# Revit family: TR2163
name_source: partatom
category: Verbindungsmittel
units: mm (PartAtom-declared; Revit-internal decimal feet)

## family parameters
Arbeitsebenenbasiert = Nein
Beim Laden mit Abzugskörper schneiden = Nein
Gemeinsam genutzt = Nein
Immer vertikal = Nein
OmniClass-Nummer = 23.25.10.27.11.21
OmniClass-Titel = Reinforcement Couplers

## types (10) — shared parameters
Endenbearbeitung 1 = Mit Gewinde
Endenbearbeitung 2 = Mit Gewinde
Hersteller = Stahlwerk Annahütte Max Aicher GmbH Co.KG
Modell = TR 2163
Stabgröße 2 = Keine
TR2163-G_Vis = Ja
TR2163-L_Vis = Ja
TR2163-SW_Vis = Ja
Typenbild = TR2163.png
Typenkommentare = TR 2163 - Ankermutter mit Bund
URL = http//:www.annahuette.com
zero-valued in all types: Einfassung Stab 2

## per-type parameters (varying)
| type | Außendurchmesser | Beschreibung | Einfassung Stab 1 | Gesamtlänge | Körper | Stabgröße 1 | TR2163-G | TR2163-L | TR2163-L1 | TR2163-Ld | TR2163-Lsw | TR2163-SW | TR2163-ø | TR2163-ød |
| TR 2163-ø18 | 36 mm  [stored 0.11811 ft] | TR2163-ø18 | 34 mm | 45 mm  [stored 0.147638 ft] | 0,31 kg | SAS 670 - ø18 | 0,31 kg | 45 mm  [stored 0.147638 ft] | 34 mm | 11 mm  [stored 0.0360892 ft] | 34 mm | 36 mm  [stored 0.11811 ft] | 42 mm  [stored 0.137795 ft] | 18 mm  [stored 0.0590551 ft] |
| TR 2163-ø22 | 41 mm  [stored 0.134514 ft] | TR2163-ø22 | 38 mm  [stored 0.124672 ft] | 50 mm  [stored 0.164042 ft] | 0,43 kg | SAS 670 - ø22 | 0,43 kg | 50 mm  [stored 0.164042 ft] | 38 mm  [stored 0.124672 ft] | 12 mm  [stored 0.0393701 ft] | 38 mm  [stored 0.124672 ft] | 41 mm  [stored 0.134514 ft] | 47 mm  [stored 0.154199 ft] | 22 mm  [stored 0.0721785 ft] |
| TR 2163-ø25 | 46 mm  [stored 0.150919 ft] | TR2163-ø25 | 40 mm  [stored 0.131234 ft] | 55 mm  [stored 0.180446 ft] | 0,59 kg | SAS 670 - ø25 | 0,59 kg | 55 mm  [stored 0.180446 ft] | 40 mm  [stored 0.131234 ft] | 15 mm  [stored 0.0492126 ft] | 40 mm  [stored 0.131234 ft] | 46 mm  [stored 0.150919 ft] | 53 mm  [stored 0.173885 ft] | 25 mm  [stored 0.082021 ft] |
| TR 2163-ø28 | 50 mm  [stored 0.164042 ft] | TR2163-ø28 | 50 mm  [stored 0.164042 ft] | 65 mm  [stored 0.213255 ft] | 0,80 kg | SAS 670 - ø28 | 0,80 kg | 65 mm  [stored 0.213255 ft] | 50 mm  [stored 0.164042 ft] | 15 mm  [stored 0.0492126 ft] | 50 mm  [stored 0.164042 ft] | 50 mm  [stored 0.164042 ft] | 58 mm  [stored 0.190289 ft] | 28 mm  [stored 0.0918635 ft] |
| TR 2163-ø30 | 55 mm  [stored 0.180446 ft] | TR2163-ø30 | 50 mm  [stored 0.164042 ft] | 65 mm  [stored 0.213255 ft] | 0,98 kg | SAS 670 - ø30 | 0,98 kg | 65 mm  [stored 0.213255 ft] | 50 mm  [stored 0.164042 ft] | 15 mm  [stored 0.0492126 ft] | 50 mm  [stored 0.164042 ft] | 55 mm  [stored 0.180446 ft] | 64 mm  [stored 0.209974 ft] | 30 mm  [stored 0.0984252 ft] |
| TR 2163-ø35 | 65 mm  [stored 0.213255 ft] | TR2163-ø35 | 53 mm  [stored 0.173885 ft] | 70 mm  [stored 0.229659 ft] | 1,51 kg | SAS 670 - ø35 | 1,51 kg | 70 mm  [stored 0.229659 ft] | 53 mm  [stored 0.173885 ft] | 17 mm | 53 mm  [stored 0.173885 ft] | 65 mm  [stored 0.213255 ft] | 75 mm | 35 mm  [stored 0.114829 ft] |
| TR 2163-ø43 | 80 mm  [stored 0.262467 ft] | TR2163-ø43 | 63 mm  [stored 0.206693 ft] | 90 mm  [stored 0.295276 ft] | 2,99 kg | SAS 670 - ø43 | 2,99 kg | 90 mm  [stored 0.295276 ft] | 63 mm  [stored 0.206693 ft] | 27 mm | 63 mm  [stored 0.206693 ft] | 80 mm  [stored 0.262467 ft] | 92 mm  [stored 0.301837 ft] | 43 mm  [stored 0.141076 ft] |
| TR 2163-ø50 | 80 mm  [stored 0.262467 ft] | TR2163-ø50 | 75 mm | 100 mm  [stored 0.328084 ft] | 2,84 kg | SAS 670 - ø50 | 2,84 kg | 100 mm  [stored 0.328084 ft] | 75 mm | 25 mm  [stored 0.082021 ft] | 75 mm | 80 mm  [stored 0.262467 ft] | 92 mm  [stored 0.301837 ft] | 50 mm  [stored 0.164042 ft] |
| TR 2163-ø57,5 | 90 mm  [stored 0.295276 ft] | TR2163-ø57,5 | 95 mm | 120 mm  [stored 0.393701 ft] | 4,15 kg | SAS 670 - ø57,5 | 4,15 kg | 120 mm  [stored 0.393701 ft] | 95 mm | 25 mm  [stored 0.082021 ft] | 95 mm | 90 mm  [stored 0.295276 ft] | 102 mm | 58 mm  [stored 0.190289 ft] |
| TR 2163-ø63,5 | 100 mm  [stored 0.328084 ft] | TR2163-ø63,5 | 117 mm  [stored 0.383858 ft] | 145 mm | 6,23 kg | SAS 670 - ø63,5 | 6,23 kg | 145 mm | 117 mm  [stored 0.383858 ft] | 28 mm  [stored 0.0918635 ft] | 117 mm  [stored 0.383858 ft] | 100 mm  [stored 0.328084 ft] | 114 mm  [stored 0.374016 ft] | 64 mm  [stored 0.209974 ft] |

note: [stored X ft] marks values corroborated as IEEE doubles in the binary element streams (Revit-internal decimal feet)
